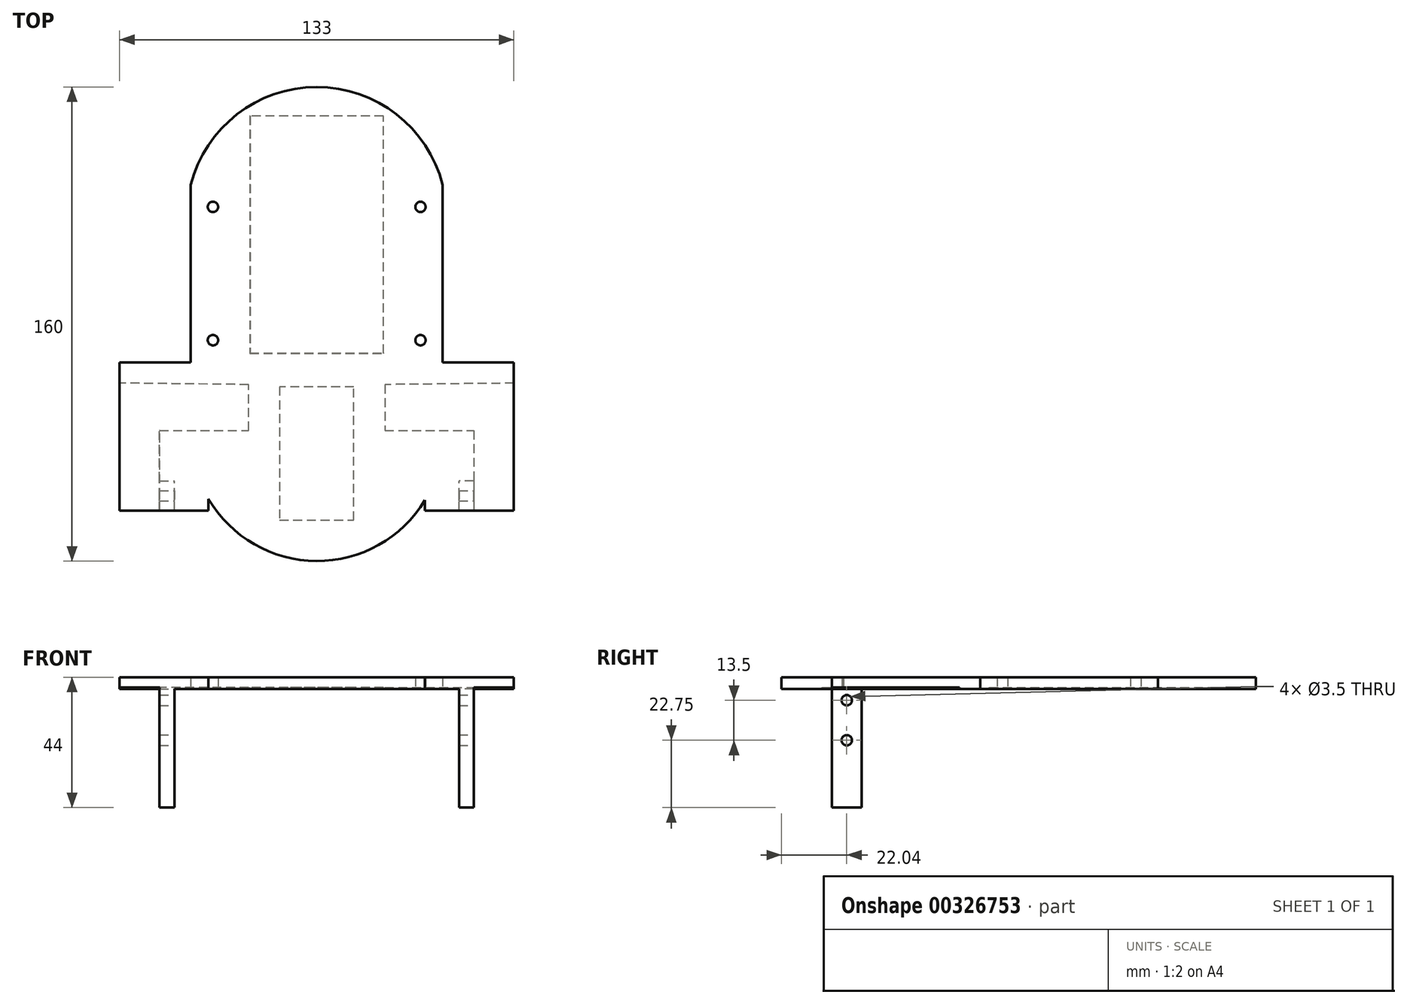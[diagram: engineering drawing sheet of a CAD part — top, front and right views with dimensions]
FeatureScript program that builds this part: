
annotation { "Feature Type Name" : "Feature", "Feature Type Description" : "" }
export const myFeature = defineFeature(function(context is Context, id is Id, definition is map)
    precondition{}
    {
        {
            var Q0;
            Q0=qCreatedBy(makeId("Top.planeOp"),FACE);
            var sketch = newSketch(context, id + "F0", { "sketchPlane" : qUnion([Q0])});
            skLineSegment(sketch, "E0.left", {"start": v(42.5, 30) * mm, "end": v(42.5, -30) * mm});
            skLineSegment(sketch, "E0.right", {"start": v(-42.5, 30) * mm, "end": v(-42.5, -30) * mm});
            skPoint(sketch, "E0.middle", {"position": v(0, 0) * mm});
            skArc(sketch, "E1", {"start": v(42.5, 30) * mm, "mid": v(0, 62.96) * mm, "end": v(-42.5, 30) * mm});
            skLineSegment(sketch, "E2.bottom", {"start": v(66.5, -30) * mm, "end": v(42.5, -30) * mm});
            skLineSegment(sketch, "E2.top", {"start": v(66.5, -80) * mm, "end": v(36.5, -80) * mm});
            skLineSegment(sketch, "E2.left", {"start": v(66.5, -30) * mm, "end": v(66.5, -80) * mm});
            skLineSegment(sketch, "E3.bottom", {"start": v(-66.5, -30) * mm, "end": v(-42.5, -30) * mm});
            skLineSegment(sketch, "E3.top", {"start": v(-66.5, -80) * mm, "end": v(-36.5, -80) * mm});
            skLineSegment(sketch, "E3.left", {"start": v(-66.5, -30) * mm, "end": v(-66.5, -80) * mm});
            skPoint(sketch, "E4.endSnap0", {"position": v(0, -30) * mm});
            skPoint(sketch, "E5.second.point", {"position": v(0, -12.04) * mm});
            skPoint(sketch, "E5.third.point", {"position": v(-39.19, -70.68) * mm});
            skArc(sketch, "E6.trimOffspring", {"start": v(-36.5, -76.09) * mm, "mid": v(-0.12, -97.04) * mm, "end": v(36.5, -76.52) * mm});
            skLineSegment(sketch, "E7.trimOffspring", {"start": v(-36.5, -76.09) * mm, "end": v(-36.5, -80) * mm});
            skLineSegment(sketch, "E8.trimOffspring", {"start": v(36.5, -76.52) * mm, "end": v(36.5, -80) * mm});
            skSolve(sketch);
        }
        {
            var Q0;
            Q0=makeQuery(id+"F0.imprint","IMPRINT",FACE,{"disambiguationData":[TD([[makeQuery(id+"F0.imprint","IMPRINT",EDGE,{"derivedFrom":sQuery(id+"F0.wireOp",EDGE,"E0.left")}),-1.0]])]});
            extrude(context, id + "F1", {"entities" : qUnion([Q0]), "depth" : 5 * mm});
        }
        {
            var Q0;
            Q0=qCreatedBy(makeId("Top.planeOp"),FACE);
            var sketch = newSketch(context, id + "F2", { "sketchPlane" : qUnion([Q0])});
            skLineSegment(sketch, "E9.bottom", {"start": v(22.5, 53.13) * mm, "end": v(-22.5, 53.13) * mm});
            skLineSegment(sketch, "E9.top", {"start": v(22.5, -26.87) * mm, "end": v(-22.5, -26.87) * mm});
            skLineSegment(sketch, "E9.left", {"start": v(22.5, 53.13) * mm, "end": v(22.5, -26.87) * mm});
            skLineSegment(sketch, "E9.right", {"start": v(-22.5, 53.13) * mm, "end": v(-22.5, -26.87) * mm});
            skPoint(sketch, "E9.middle", {"position": v(0, 13.13) * mm});
            skLineSegment(sketch, "E10.bottom", {"start": v(12.5, -38.23) * mm, "end": v(-12.5, -38.23) * mm});
            skLineSegment(sketch, "E10.top", {"start": v(12.5, -83.23) * mm, "end": v(-12.5, -83.23) * mm});
            skLineSegment(sketch, "E10.left", {"start": v(12.5, -38.23) * mm, "end": v(12.5, -83.23) * mm});
            skLineSegment(sketch, "E10.right", {"start": v(-12.5, -38.23) * mm, "end": v(-12.5, -83.23) * mm});
            skPoint(sketch, "E10.middle", {"position": v(0, -60.73) * mm});
            skSolve(sketch);
        }
        {
            var Q0;
            Q0=makeQuery(id+"F1.opExtrude","CAP_FACE",FACE,{"disambiguationData":[OSD([sQuery(id+"F0.wireOp",EDGE,"E0.left"),sQuery(id+"F0.wireOp",EDGE,"E0.right"),sQuery(id+"F0.wireOp",EDGE,"E1"),sQuery(id+"F0.wireOp",EDGE,"E2.top"),sQuery(id+"F0.wireOp",EDGE,"E2.left"),sQuery(id+"F0.wireOp",EDGE,"E2.bottom"),sQuery(id+"F0.wireOp",EDGE,"E3.top"),sQuery(id+"F0.wireOp",EDGE,"E3.left"),sQuery(id+"F0.wireOp",EDGE,"E3.bottom"),sQuery(id+"F0.wireOp",EDGE,"E6.trimOffspring"),sQuery(id+"F0.wireOp",EDGE,"E7.trimOffspring"),sQuery(id+"F0.wireOp",EDGE,"E8.trimOffspring")])],"isStart":false});
            var Q1;
            Q1=qSketchRegion(id+"F2",true);
            extrude(context, id + "F3", {"entities" : qUnion([Q0, Q1]), "operationType" : NewBodyOperationType.REMOVE, "endBound" : BoundingType.SYMMETRIC, "oppositeDirection" : true, "depth" : 1 * mm, "hasDraft" : true, "draftAngle" : 3 * degree});
        }
        {
            var Q0;
            Q0=qCreatedBy(makeId("Top.planeOp"),FACE);
            var sketch = newSketch(context, id + "F4", { "sketchPlane" : qUnion([Q0])});
            skLineSegment(sketch, "E11.top", {"start": v(66.5, -80) * mm, "end": v(53, -80) * mm});
            skLineSegment(sketch, "E11.left", {"start": v(66.5, -37) * mm, "end": v(66.5, -80) * mm});
            skLineSegment(sketch, "E11.right", {"start": v(53, -53) * mm, "end": v(53, -80) * mm});
            skPoint(sketch, "E11.middle", {"position": v(59.75, -58.5) * mm});
            skLineSegment(sketch, "E12.top", {"start": v(-53, -80) * mm, "end": v(-66.5, -80) * mm});
            skLineSegment(sketch, "E12.left", {"start": v(-53, -53) * mm, "end": v(-53, -80) * mm});
            skLineSegment(sketch, "E12.right", {"start": v(-66.5, -37) * mm, "end": v(-66.5, -80) * mm});
            skPoint(sketch, "E12.middle", {"position": v(-59.75, -58.5) * mm});
            skLineSegment(sketch, "E13.top", {"start": v(53, -53) * mm, "end": v(23, -53) * mm});
            skLineSegment(sketch, "E13.left", {"start": v(66.5, -37) * mm, "end": v(66.5, -53) * mm});
            skLineSegment(sketch, "E13.right", {"start": v(23, -37.5) * mm, "end": v(23, -53) * mm});
            skLineSegment(sketch, "E14.top", {"start": v(-53, -53) * mm, "end": v(-23, -53) * mm});
            skLineSegment(sketch, "E14.left", {"start": v(-66.5, -37) * mm, "end": v(-66.5, -53) * mm});
            skLineSegment(sketch, "E14.right", {"start": v(-23, -37.5) * mm, "end": v(-23, -53) * mm});
            skPoint(sketch, "E14.bottom.start.orphan", {"position": v(-53, -37) * mm});
            skLineSegment(sketch, "E15", {"start": v(-66.5, -37) * mm, "end": v(-23, -37.5) * mm});
            skPoint(sketch, "E11.bottom.end.orphan", {"position": v(53, -37) * mm});
            skLineSegment(sketch, "E16", {"start": v(23, -37.5) * mm, "end": v(66.5, -37) * mm});
            skSolve(sketch);
        }
        {
            var Q0;
            Q0=makeQuery(id+"F3.boolean.opBoolean","COPY",FACE,{"derivedFrom":makeQuery(id+"F3.opExtrude","CAP_FACE",FACE,{"disambiguationData":[OSD([sQuery(id+"F0.wireOp",EDGE,"E0.left"),sQuery(id+"F0.wireOp",EDGE,"E0.right"),sQuery(id+"F0.wireOp",EDGE,"E1"),sQuery(id+"F0.wireOp",EDGE,"E2.top"),sQuery(id+"F0.wireOp",EDGE,"E2.left"),sQuery(id+"F0.wireOp",EDGE,"E2.bottom"),sQuery(id+"F0.wireOp",EDGE,"E3.top"),sQuery(id+"F0.wireOp",EDGE,"E3.left"),sQuery(id+"F0.wireOp",EDGE,"E3.bottom"),sQuery(id+"F0.wireOp",EDGE,"E6.trimOffspring"),sQuery(id+"F0.wireOp",EDGE,"E7.trimOffspring"),sQuery(id+"F0.wireOp",EDGE,"E8.trimOffspring")])],"isStart":false})});
            var Q1;
            Q1=qSketchRegion(id+"F4",true);
            extrude(context, id + "F5", {"entities" : qUnion([Q0, Q1]), "operationType" : NewBodyOperationType.REMOVE, "endBound" : BoundingType.SYMMETRIC, "oppositeDirection" : true, "depth" : 1 * mm, "hasDraft" : true, "draftAngle" : 3 * degree, "hasSecondDirection" : true, "secondDirectionOppositeDirection" : false, "secondDirectionDepth" : 25 * mm});
        }
        {
            var Q0;
            Q0=qCreatedBy(makeId("Top.planeOp"),FACE);
            var sketch = newSketch(context, id + "F6", { "sketchPlane" : qUnion([Q0])});
            skLineSegment(sketch, "E17.bottom", {"start": v(-53, -80) * mm, "end": v(-48, -80) * mm});
            skLineSegment(sketch, "E17.left", {"start": v(-53, -80) * mm, "end": v(-53, -70) * mm});
            skLineSegment(sketch, "E17.right", {"start": v(-48, -80) * mm, "end": v(-48, -70) * mm});
            skLineSegment(sketch, "E18.bottom", {"start": v(53, -80) * mm, "end": v(48, -80) * mm});
            skLineSegment(sketch, "E18.top", {"start": v(53, -70) * mm, "end": v(48, -70) * mm});
            skLineSegment(sketch, "E18.left", {"start": v(53, -80) * mm, "end": v(53, -70) * mm});
            skLineSegment(sketch, "E18.right", {"start": v(48, -80) * mm, "end": v(48, -70) * mm});
            skLineSegment(sketch, "E19", {"start": v(-53, -70) * mm, "end": v(-48, -70) * mm});
            skSolve(sketch);
        }
        {
            var Q0;
            Q0 = qSketchRegion(id + "F6", true);
            extrude(context, id + "F7", {"entities" : qUnion([Q0]), "operationType" : NewBodyOperationType.ADD, "oppositeDirection" : true, "depth" : 40 * mm});
        }
        {
            var Q0;
            Q0=qCreatedBy(makeId("Top.planeOp"),FACE);
            var sketch = newSketch(context, id + "F8", { "sketchPlane" : qUnion([Q0])});
            skPoint(sketch, "E20.middle", {"position": v(-35, -22.5) * mm});
            skPoint(sketch, "E21.middle", {"position": v(35, -22.5) * mm});
            skPoint(sketch, "E22.middle", {"position": v(35, 22.5) * mm});
            skPoint(sketch, "E23.middle", {"position": v(-35, 22.5) * mm});
            skCircle(sketch, "E24", {"center": v(-35, -22.5) * mm, "radius": 1.75 * mm});
            skCircle(sketch, "E25", {"center": v(35, -22.5) * mm, "radius": 1.75 * mm});
            skCircle(sketch, "E26", {"center": v(-35, 22.5) * mm, "radius": 1.75 * mm});
            skCircle(sketch, "E27", {"center": v(35, 22.5) * mm, "radius": 1.75 * mm});
            skSolve(sketch);
        }
        {
            var Q0;
            Q0 = qSketchRegion(id + "F8", true);
            extrude(context, id + "F9", {"entities" : qUnion([Q0]), "operationType" : NewBodyOperationType.REMOVE, "depth" : 25 * mm});
        }
        {
            var Q0;
            Q0=makeQuery(id+"F7.opExtrude","SWEPT_FACE",FACE,{"disambiguationData":[OSD([sQuery(id+"F6.wireOp",EDGE,"E18.left")])]});
            var sketch = newSketch(context, id + "F10", { "sketchPlane" : qUnion([Q0])});
            skCircle(sketch, "E28", {"center": v(-75, -3.75) * mm, "radius": 1.75 * mm});
            skCircle(sketch, "E29", {"center": v(-75, -17.25) * mm, "radius": 1.75 * mm});
            skSolve(sketch);
        }
        {
            var Q0;
            Q0 = qSketchRegion(id + "F10", true);
            extrude(context, id + "F11", {"entities" : qUnion([Q0]), "operationType" : NewBodyOperationType.REMOVE, "oppositeDirection" : true, "depth" : 200 * mm});
        }
    });
